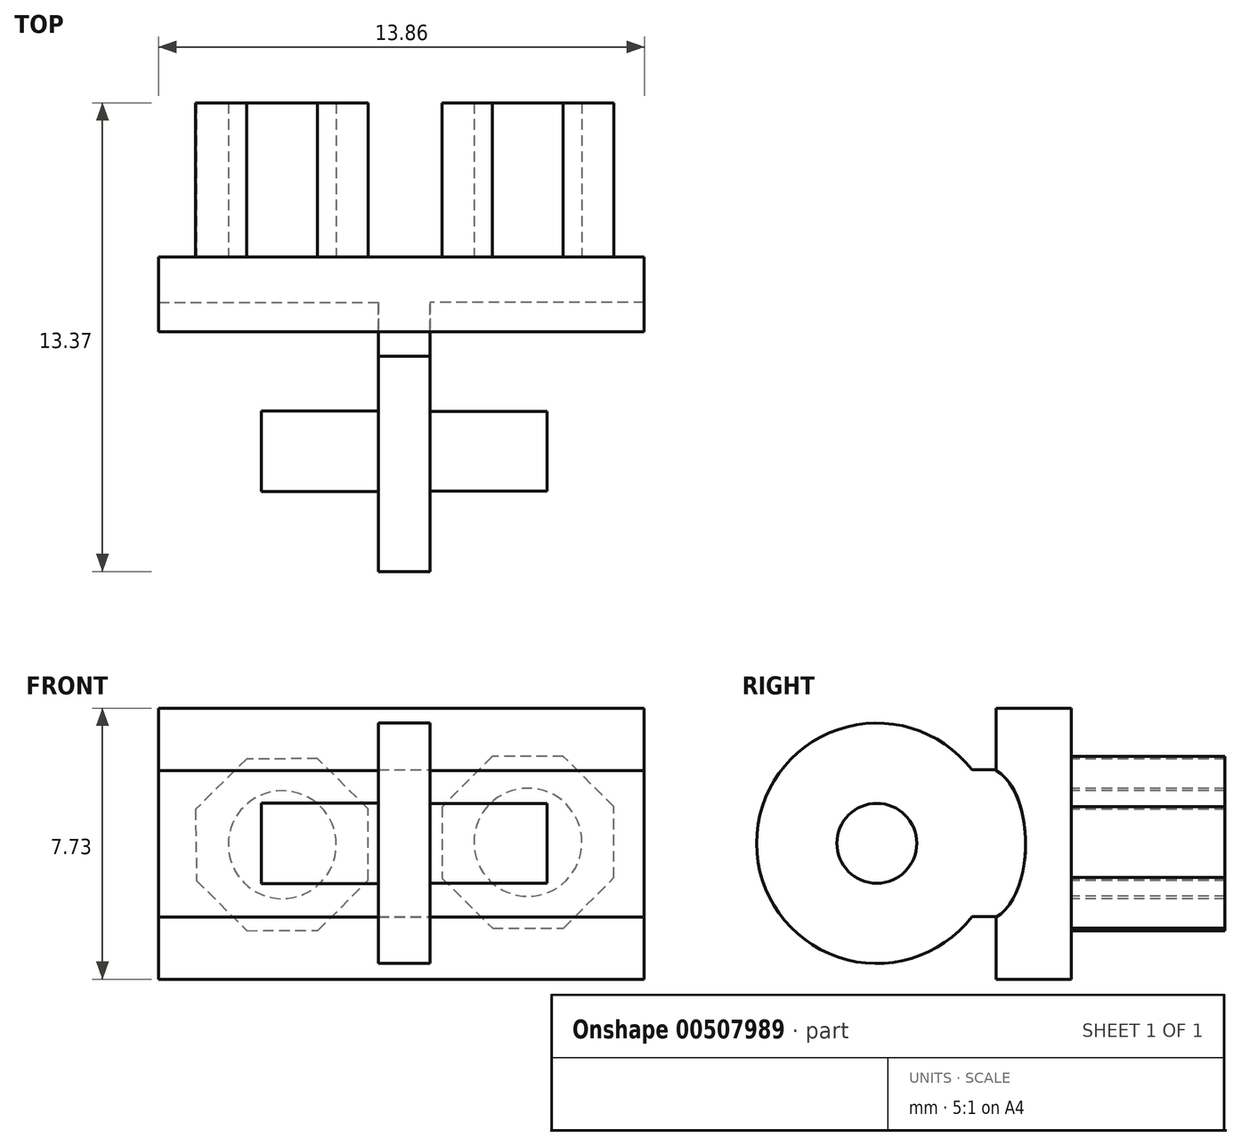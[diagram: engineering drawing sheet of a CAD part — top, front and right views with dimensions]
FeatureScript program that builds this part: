
annotation { "Feature Type Name" : "Feature", "Feature Type Description" : "" }
export const myFeature = defineFeature(function(context is Context, id is Id, definition is map)
    precondition{}
    {
        {
            var Q0;
            Q0=qCreatedBy(makeId("Front.planeOp"),FACE);
            var sketch = newSketch(context, id + "F0", { "sketchPlane" : qUnion([Q0])});
            skLineSegment(sketch, "E0.bottom", {"start": v(-6.27, 10.43) * mm, "end": v(7.59, 10.43) * mm});
            skLineSegment(sketch, "E0.top", {"start": v(-6.27, 2.7) * mm, "end": v(7.59, 2.7) * mm});
            skLineSegment(sketch, "E0.left", {"start": v(-6.27, 10.43) * mm, "end": v(-6.27, 2.7) * mm});
            skLineSegment(sketch, "E0.right", {"start": v(7.59, 10.43) * mm, "end": v(7.59, 2.7) * mm});
            skSolve(sketch);
        }
        {
            var Q0;
            Q0 = qSketchRegion(id + "F0", true);
            extrude(context, id + "F1", {"entities" : qUnion([Q0]), "depth" : 2.14 * mm, "offsetDistance" : 25 * mm});
        }
        {
            var Q0;
            Q0=makeQuery(id+"F1.opExtrude","SWEPT_FACE",FACE,{"disambiguationData":[OSD([sQuery(id+"F0.wireOp",EDGE,"E0.right")])]});
            var sketch = newSketch(context, id + "F2", { "sketchPlane" : qUnion([Q0])});
            skPoint(sketch, "E1", {"position": v(-2.14, 8.66) * mm});
            skPoint(sketch, "E2", {"position": v(-2.14, 4.47) * mm});
            skPoint(sketch, "E3.2.internal.snap0", {"position": v(-2.14, 6.56) * mm});
            skFitSpline(sketch, "E3", {"points": [v(-2.14, 4.47) * mm, v(-2.14, 8.66) * mm, v(-5.28, 6.56) * mm, v(-2.14, 4.47) * mm]});
            skPoint(sketch, "E4", {"position": v(-1.32, 6.56) * mm});
            skSolve(sketch);
        }
        {
            var Q0;
            Q0 = qSketchRegion(id + "F2", true);
            extrude(context, id + "F3", {"entities" : qUnion([Q0]), "operationType" : NewBodyOperationType.REMOVE, "endBound" : BoundingType.THROUGH_ALL, "oppositeDirection" : true, "depth" : 25 * mm, "offsetDistance" : 25 * mm});
        }
        {
            var Q0;
            Q0=qCreatedBy(makeId("Right.planeOp"),FACE);
            var sketch = newSketch(context, id + "F4", { "sketchPlane" : qUnion([Q0])});
            skLineSegment(sketch, "E5", {"start": v(-2.04, 4.48) * mm, "end": v(-3.76, 4.48) * mm});
            skLineSegment(sketch, "E6", {"start": v(-2.04, 8.67) * mm, "end": v(-3.76, 8.67) * mm});
            skLineSegment(sketch, "E7", {"start": v(-3.76, 4.48) * mm, "end": v(-3.76, 8.67) * mm});
            skLineSegment(sketch, "E8", {"start": v(-2.04, 8.67) * mm, "end": v(-2.04, 4.48) * mm});
            skLineSegment(sketch, "E9", {"start": v(-2.04, 4.48) * mm, "end": v(-1.05, 4.48) * mm});
            skLineSegment(sketch, "E10", {"start": v(-1.05, 4.48) * mm, "end": v(-1.05, 8.75) * mm});
            skLineSegment(sketch, "E11", {"start": v(-1.05, 8.75) * mm, "end": v(-2.04, 8.67) * mm});
            skSolve(sketch);
        }
        {
            var Q0;
            Q0 = qSketchRegion(id + "F4", true);
            extrude(context, id + "F5", {"entities" : qUnion([Q0]), "operationType" : NewBodyOperationType.ADD, "depth" : 1.48 * mm, "offsetDistance" : 25 * mm});
        }
        {
            var Q0;
            Q0=makeQuery(id+"F5.opExtrude","CAP_FACE",FACE,{"disambiguationData":[OSD([sQuery(id+"F4.wireOp",EDGE,"E5"),sQuery(id+"F4.wireOp",EDGE,"E6"),sQuery(id+"F4.wireOp",EDGE,"E7"),sQuery(id+"F4.wireOp",EDGE,"E9"),sQuery(id+"F4.wireOp",EDGE,"E10"),sQuery(id+"F4.wireOp",EDGE,"E11")])],"isStart":false});
            var sketch = newSketch(context, id + "F6", { "sketchPlane" : qUnion([Q0])});
            skCircle(sketch, "E12", {"center": v(-5.55, 6.58) * mm, "radius": 3.43 * mm});
            skPoint(sketch, "E12.centerSnap0", {"position": v(-3.76, 6.58) * mm});
            skSolve(sketch);
        }
        {
            var Q0;
            Q0 = qSketchRegion(id + "F6", true);
            extrude(context, id + "F7", {"entities" : qUnion([Q0]), "operationType" : NewBodyOperationType.ADD, "oppositeDirection" : true, "depth" : 1.48 * mm, "offsetDistance" : 25 * mm});
        }
        {
            var Q0;
            Q0=makeQuery(id+"F7.boolean.opBoolean","MERGE",FACE,{"derivedFrom":[makeQuery(id+"F5.opExtrude","CAP_FACE",FACE,{"disambiguationData":[OSD([sQuery(id+"F4.wireOp",EDGE,"E5"),sQuery(id+"F4.wireOp",EDGE,"E6"),sQuery(id+"F4.wireOp",EDGE,"E7"),sQuery(id+"F4.wireOp",EDGE,"E9"),sQuery(id+"F4.wireOp",EDGE,"E10"),sQuery(id+"F4.wireOp",EDGE,"E11")])],"isStart":false}),makeQuery(id+"F7.opExtrude","CAP_FACE",FACE,{"disambiguationData":[OSD([sQuery(id+"F6.wireOp",EDGE,"E12")])],"isStart":true})]});
            var sketch = newSketch(context, id + "F8", { "sketchPlane" : qUnion([Q0])});
            skCircle(sketch, "E13", {"center": v(-5.55, 6.58) * mm, "radius": 1.14 * mm});
            skSolve(sketch);
        }
        {
            var Q0;
            Q0=makeQuery(id+"F7.boolean.opBoolean","MERGE",FACE,{"derivedFrom":[makeQuery(id+"F5.opExtrude","CAP_FACE",FACE,{"disambiguationData":[OSD([sQuery(id+"F4.wireOp",EDGE,"E5"),sQuery(id+"F4.wireOp",EDGE,"E6"),sQuery(id+"F4.wireOp",EDGE,"E7"),sQuery(id+"F4.wireOp",EDGE,"E9"),sQuery(id+"F4.wireOp",EDGE,"E10"),sQuery(id+"F4.wireOp",EDGE,"E11")])],"isStart":true}),makeQuery(id+"F7.opExtrude","CAP_FACE",FACE,{"disambiguationData":[OSD([sQuery(id+"F6.wireOp",EDGE,"E12")])],"isStart":false})]});
            var sketch = newSketch(context, id + "F9", { "sketchPlane" : qUnion([Q0])});
            skCircle(sketch, "E14", {"center": v(5.55, 6.58) * mm, "radius": 1.15 * mm});
            skSolve(sketch);
        }
        {
            var Q0;
            Q0=makeQuery(id+"F8.imprint","IMPRINT",FACE,{"disambiguationData":[TD([[makeQuery(id+"F8.imprint","IMPRINT",EDGE,{"derivedFrom":sQuery(id+"F8.wireOp",EDGE,"E13")}),1.0]])]});
            var Q1;
            Q1=sQuery(id+"F8.wireOp",EDGE,"E13");
            extrude(context, id + "F10", {"entities" : qUnion([Q0]), "operationType" : NewBodyOperationType.ADD, "surfaceEntities" : qUnion([Q1]), "depth" : 3.34 * mm, "offsetDistance" : 25 * mm});
        }
        {
            var Q0;
            Q0 = qSketchRegion(id + "F9", true);
            extrude(context, id + "F11", {"entities" : qUnion([Q0]), "operationType" : NewBodyOperationType.ADD, "depth" : 3.34 * mm, "offsetDistance" : 25 * mm});
        }
        {
            var Q0;
            Q0=makeQuery(id+"F1.opExtrude","CAP_FACE",FACE,{"disambiguationData":[OSD([sQuery(id+"F0.wireOp",EDGE,"E0.bottom"),sQuery(id+"F0.wireOp",EDGE,"E0.top"),sQuery(id+"F0.wireOp",EDGE,"E0.left"),sQuery(id+"F0.wireOp",EDGE,"E0.right")])],"isStart":true});
            var sketch = newSketch(context, id + "F12", { "sketchPlane" : qUnion([Q0])});
            skCircle(sketch, "E15.cCircle", {"center": v(-4.27, 6.6) * mm, "radius": 2.45 * mm, "construction": true});
            skLineSegment(sketch, "E15.0", {"start": v(-3.25, 9.05) * mm, "end": v(-1.81, 7.61) * mm});
            skLineSegment(sketch, "E15.1", {"start": v(-1.81, 7.61) * mm, "end": v(-1.82, 5.58) * mm});
            skLineSegment(sketch, "E15.2", {"start": v(-1.82, 5.58) * mm, "end": v(-3.26, 4.15) * mm});
            skLineSegment(sketch, "E15.3", {"start": v(-3.26, 4.15) * mm, "end": v(-5.29, 4.16) * mm});
            skLineSegment(sketch, "E15.4", {"start": v(-5.29, 4.16) * mm, "end": v(-6.72, 5.6) * mm});
            skLineSegment(sketch, "E15.5", {"start": v(-6.72, 5.6) * mm, "end": v(-6.71, 7.63) * mm});
            skLineSegment(sketch, "E15.6", {"start": v(-6.71, 7.63) * mm, "end": v(-5.28, 9.06) * mm});
            skLineSegment(sketch, "E15.7", {"start": v(-5.28, 9.06) * mm, "end": v(-3.25, 9.05) * mm});
            skPoint(sketch, "E15.0.midPoint", {"position": v(-2.53, 8.33) * mm});
            skPoint(sketch, "E16.startSnap0", {"position": v(-7.59, 6.56) * mm});
            skPoint(sketch, "E16.endSnap0", {"position": v(-7.59, 6.56) * mm});
            skPoint(sketch, "E17.1.0.0", {"position": v(4.48, 8.26) * mm});
            skPoint(sketch, "E17.1.0.1", {"position": v(-0.58, 6.5) * mm});
            skCircle(sketch, "E17.1.0.2", {"center": v(2.74, 6.54) * mm, "radius": 2.45 * mm, "construction": true});
            skLineSegment(sketch, "E17.1.0.3", {"start": v(0.3, 7.56) * mm, "end": v(1.73, 8.99) * mm});
            skLineSegment(sketch, "E17.1.0.4", {"start": v(3.75, 4.08) * mm, "end": v(1.72, 4.09) * mm});
            skLineSegment(sketch, "E17.1.0.5", {"start": v(3.76, 8.98) * mm, "end": v(5.22, 7.54) * mm});
            skLineSegment(sketch, "E17.1.0.6", {"start": v(0.29, 5.53) * mm, "end": v(0.3, 7.56) * mm});
            skLineSegment(sketch, "E17.1.0.7", {"start": v(1.72, 4.1) * mm, "end": v(0.29, 5.53) * mm});
            skPoint(sketch, "E17.1.0.8", {"position": v(-0.58, 6.5) * mm});
            skLineSegment(sketch, "E17.1.0.9", {"start": v(1.73, 8.99) * mm, "end": v(3.76, 8.98) * mm});
            skLineSegment(sketch, "E17.1.0.10", {"start": v(5.19, 5.52) * mm, "end": v(3.75, 4.08) * mm});
            skLineSegment(sketch, "E17.1.0.11", {"start": v(5.22, 7.54) * mm, "end": v(5.19, 5.52) * mm});
            skLineSegment(sketch, "E17.direction1", {"start": v(-5.29, 4.16) * mm, "end": v(1.72, 4.1) * mm, "construction": true});
            skCircle(sketch, "E18", {"center": v(-4.27, 6.6) * mm, "radius": 1.54 * mm});
            skCircle(sketch, "E19", {"center": v(2.74, 6.54) * mm, "radius": 1.54 * mm});
            skSolve(sketch);
        }
        {
            var Q0;
            Q0 = qSketchRegion(id + "F12", true);
            extrude(context, id + "F13", {"entities" : qUnion([Q0]), "operationType" : NewBodyOperationType.ADD, "depth" : 4.39 * mm, "offsetDistance" : 25 * mm});
        }
    });
